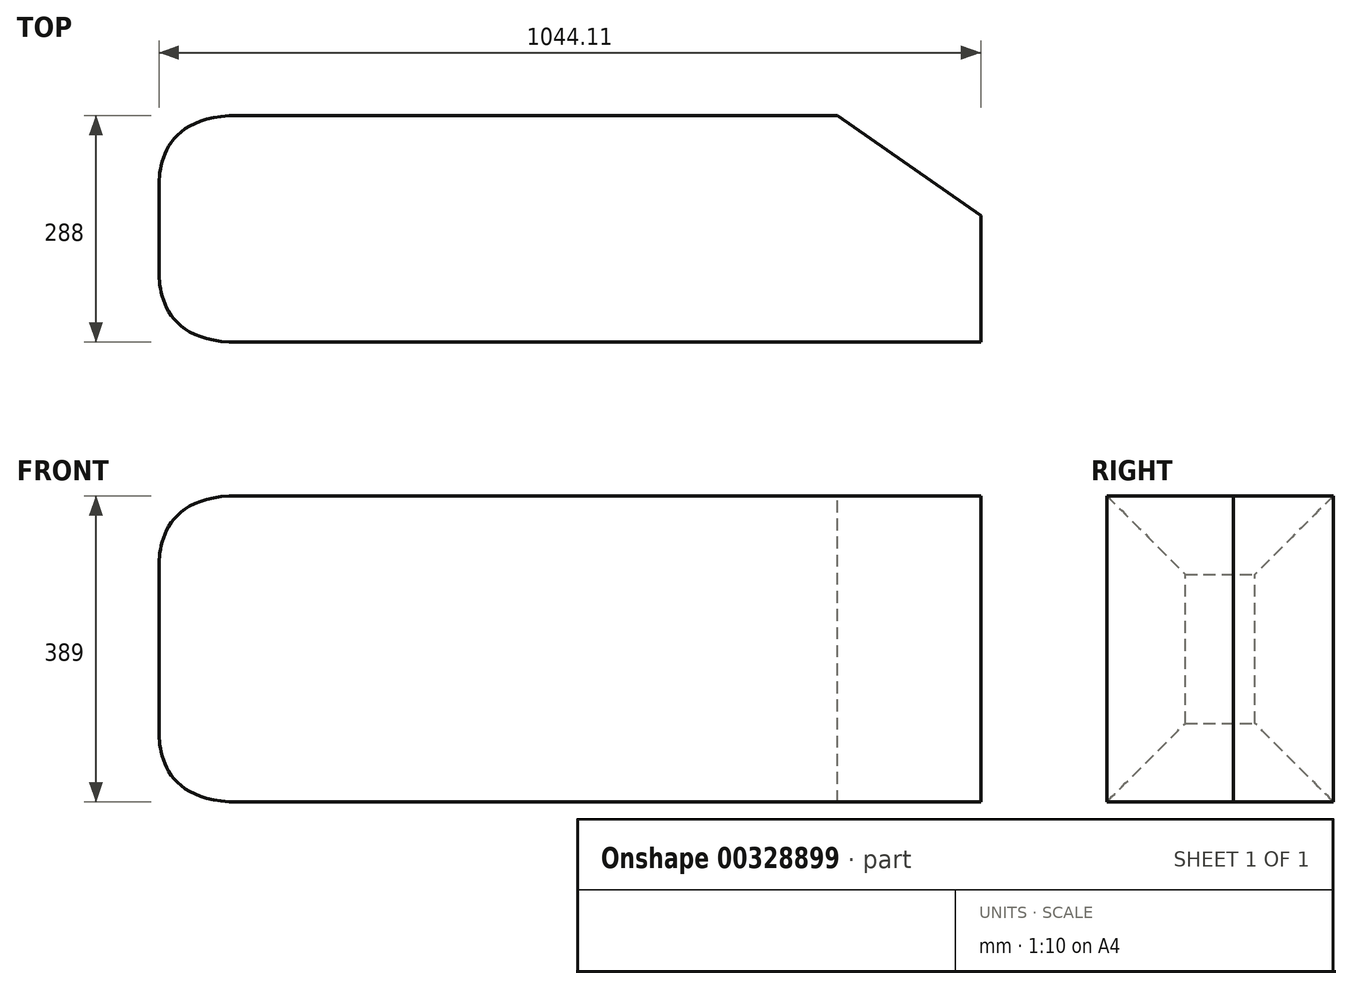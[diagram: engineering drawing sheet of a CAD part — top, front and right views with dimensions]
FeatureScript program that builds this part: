
annotation { "Feature Type Name" : "Feature", "Feature Type Description" : "" }
export const myFeature = defineFeature(function(context is Context, id is Id, definition is map)
    precondition{}
    {
        {
            var Q0;
            Q0=qCreatedBy(makeId("Top.planeOp"),FACE);
            var sketch = newSketch(context, id + "F0", { "sketchPlane" : qUnion([Q0])});
            skLineSegment(sketch, "E0", {"start": v(0, 50) * mm, "end": v(-944, 50) * mm});
            skLineSegment(sketch, "E1", {"start": v(-944, 50) * mm, "end": v(-944, 338) * mm});
            skLineSegment(sketch, "E2", {"start": v(-944, 338) * mm, "end": v(-181.85, 338) * mm});
            skLineSegment(sketch, "E3", {"start": v(0, 50) * mm, "end": v(0, 210.67) * mm});
            skLineSegment(sketch, "E4", {"start": v(0, 210.67) * mm, "end": v(-181.85, 338) * mm});
            skPoint(sketch, "E5", {"position": v(-944, 238) * mm});
            skPoint(sketch, "E6", {"position": v(-944, 150) * mm});
            skSolve(sketch);
        }
        {
            var Q0;
            Q0 = qSketchRegion(id + "F0", true);
            extrude(context, id + "F1", {"entities" : qUnion([Q0]), "oppositeDirection" : true, "depth" : 389 * mm});
        }
        {
            var Q0;
            Q0=makeQuery(id+"F1.opExtrude","SWEPT_FACE",FACE,{"disambiguationData":[OSD([sQuery(id+"F0.wireOp",EDGE,"E1")])]});
            cPlane(context, id + "F2", {"entities" : qUnion([Q0]), "cplaneType" : CPlaneType.OFFSET, "offset" : 100 * mm, "width" : 150 * mm, "height" : 150 * mm});
        }
        {
            var Q0;
            Q0=qCreatedBy(id+"F2.planeOp",FACE);
            var sketch = newSketch(context, id + "F3", { "sketchPlane" : qUnion([Q0])});
            skLineSegment(sketch, "E7.bottom", {"start": v(-150, -289) * mm, "end": v(-238, -289) * mm});
            skLineSegment(sketch, "E7.top", {"start": v(-150, -100) * mm, "end": v(-238, -100) * mm});
            skLineSegment(sketch, "E7.left", {"start": v(-150, -289) * mm, "end": v(-150, -100) * mm});
            skLineSegment(sketch, "E7.right", {"start": v(-238, -289) * mm, "end": v(-238, -100) * mm});
            skSolve(sketch);
        }
        {
            var Q1;
            Q1=makeQuery(id+"F1.opExtrude","SWEPT_FACE",FACE,{"disambiguationData":[OSD([sQuery(id+"F0.wireOp",EDGE,"E1")])]});
            var Q2;
            Q2=makeQuery(id+"F3.imprint","IMPRINT",FACE,{"disambiguationData":[TD([[makeQuery(id+"F3.imprint","IMPRINT",EDGE,{"derivedFrom":sQuery(id+"F3.wireOp",EDGE,"E7.bottom")}),-1.0]])]});
            var Q3;
            Q3=sQuery(id+"F3.wireOp",VERTEX,"E7.left.end");
            loft(context, id + "F4", {"operationType" : NewBodyOperationType.ADD, "startCondition" : LoftEndDerivativeType.MATCH_TANGENT, "startMagnitude" : 3, "endCondition" : LoftEndDerivativeType.TANGENT_TO_PROFILE, "endMagnitude" : .5, "sheetProfilesArray" : [{ "sheetProfileEntities" : qUnion([Q1]) }, { "sheetProfileEntities" : qUnion([Q2]) }], "connections" : [{ "connectionEntities" : qUnion([Q3]), "connectionEdgeQueries" : qUnion([]), "connectionEdgeParameters" : [] }]});
        }
    });
